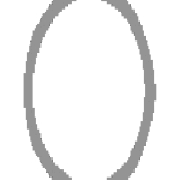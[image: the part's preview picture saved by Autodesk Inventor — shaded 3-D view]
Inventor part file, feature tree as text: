
AUTODESK INVENTOR PART (.ipt)
format: ipt  version: 2021 (Build 250183000, 183)  size: 110,592 bytes
history: native  units: in
note: dims shown in document units (in); Inventor stores cm internally (conversion verified against a paired STEP export)
features: other x4, sketch x3, plane x1
ambient origin geometry x8: Origin, YZ Plane, XZ Plane, XY Plane, X Axis, Y Axis, Z Axis, Center Point
bodies: Solid1 (feature_tree), Body (feature_tree)
feature tree (8):
  other  "Driven Length"
  other  "Frame Generator"
  other  "Start Plane"
  other  "End Plane"
  sketch  "Sketch"  dims[d2=8.0in d4=-0.0in d5=8.0in d6=0.12in d7=0.0in d8=90.0deg d9=8.0in]
  sketch  "Sketch2"  dims[d0=1.0in]
  plane  "Work Plane3"
  sketch  "Sketch3"  dims[d1=0.065in]
